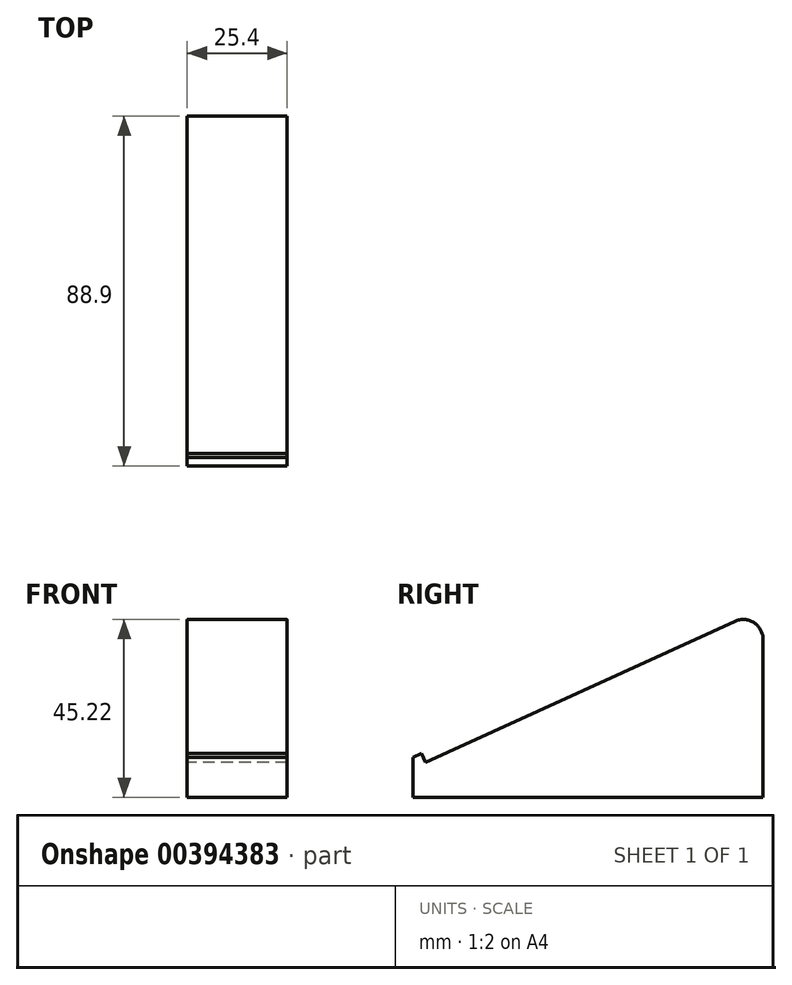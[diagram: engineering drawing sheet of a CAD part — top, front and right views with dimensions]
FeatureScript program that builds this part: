
annotation { "Feature Type Name" : "Feature", "Feature Type Description" : "" }
export const myFeature = defineFeature(function(context is Context, id is Id, definition is map)
    precondition{}
    {
        {
            var Q0;
            Q0=qCreatedBy(makeId("Right.planeOp"),FACE);
            var sketch = newSketch(context, id + "F0", { "sketchPlane" : qUnion([Q0])});
            skLineSegment(sketch, "E0.top", {"start": v(-44.45, -25.4) * mm, "end": v(44.45, -25.4) * mm});
            skLineSegment(sketch, "E0.left", {"start": v(-44.45, -15.24) * mm, "end": v(-44.45, -25.4) * mm});
            skLineSegment(sketch, "E0.right", {"start": v(44.45, 22.65) * mm, "end": v(44.45, -25.4) * mm});
            skPoint(sketch, "E0.middle", {"position": v(0, 0) * mm});
            skLineSegment(sketch, "E1", {"start": v(-44.45, -15.24) * mm, "end": v(-42.3, -14.26) * mm});
            skLineSegment(sketch, "E2", {"start": v(-42.3, -14.26) * mm, "end": v(-41.26, -16.53) * mm});
            skLineSegment(sketch, "E3", {"start": v(-41.26, -16.53) * mm, "end": v(24.8, 13.67) * mm});
            skPoint(sketch, "E4.orphan", {"position": v(-44.45, 25.4) * mm});
            skLineSegment(sketch, "E5", {"start": v(24.8, 13.67) * mm, "end": v(44.45, 22.65) * mm});
            skPoint(sketch, "E6.orphan", {"position": v(44.45, 25.4) * mm});
            skSolve(sketch);
        }
        {
            var Q0;
            Q0=makeQuery(id+"F0.imprint","IMPRINT",FACE,{"disambiguationData":[TD([[makeQuery(id+"F0.imprint","IMPRINT",EDGE,{"derivedFrom":sQuery(id+"F0.wireOp",EDGE,"E0.top")}),1.0]])]});
            extrude(context, id + "F1", {"entities" : qUnion([Q0]), "depth" : 25.4 * mm, "offsetDistance" : 25.4 * mm});
        }
        {
            var Q0;
            Q0=makeQuery(id+"F1.opExtrude","SWEPT_EDGE",EDGE,{"disambiguationData":[OSD([sQuery(id+"F0.wireOp",EDGE,"E0.right"),sQuery(id+"F0.wireOp",EDGE,"E5")])]});
            fillet(context, id + "F2", {"entities" : qUnion([Q0]), "radius" : 5.08 * mm, "tangentPropagation" : true, "allowEdgeOverflow" : false});
        }
    });
